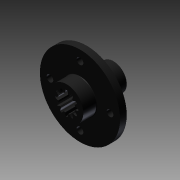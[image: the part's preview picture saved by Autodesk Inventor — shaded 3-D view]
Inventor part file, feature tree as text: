
AUTODESK INVENTOR PART (.ipt)
format: ipt  version: 2011 (Build 150239000, 239)  size: 213,504 bytes
history: native  units: mm (DEFAULTED — no unit token found)
features: sketch x8, extrude x5, hole x3, pattern_circular x1, fillet x1
ambient origin geometry x8: Origin, YZ Plane, XZ Plane, XY Plane, X Axis, Y Axis, Z Axis, Center Point
bodies: Solid1 (feature_tree)
feature tree (18):
  extrude  "Extrusion1"  Depth=76.2mm
  hole  "Mounting Hole"  [1 undecoded]
  pattern_circular  "Circular Pattern1"  Count=4 Angle=360.0deg
  extrude  "Extrusion4"  Depth=12.7mm TaperAngle=0.0deg
  extrude  "Extrusion5"  Depth=29.845mm
  hole  "Hole2"  [1 undecoded]
  extrude  "Extrusion2"  Depth=10.31875mm
  hole  "Hole3"  [1 undecoded]
  extrude  "Extrusion3"  [1 undecoded]
  fillet  "Fillet1"  [1 undecoded]
  sketch  "Sketch1"  dims[d0=6.35mm d1=0.0mm d2=76.2mm]
  sketch  "Sketch2"  dims[d3=0.0mm d4=28.575mm]
  sketch  "Sketch3"  dims[d5=6.35mm d6=12.7mm d7=9.525mm d8=6.35mm d9=14.3117mm d10=19.05mm d11=20.594885mm d12=40.0mm d14=360.0deg]
  sketch  "Sketch4"  dims[d15=31.75mm d17=12.7mm d18=0.0mm]
  sketch  "Sketch5"  dims[d22=12.7mm d23=0.0mm d27=29.845mm]
  sketch  "Sketch6"  dims[d28=25.4mm d29=-0.872665mm d31=16.0mm]
  sketch  "Sketch7"  dims[d32=4.7625mm d33=10.31875mm]
  sketch  "Sketch8"  dims[d34=28.575mm d35=0.0mm d36=9.525mm d37=12.7mm d38=9.525mm d39=6.35mm d40=14.3117mm d41=19.05mm d42=20.594885mm d43=0.508mm d49=16.2mm d50=12.7mm d51=9.525mm d52=6.35mm d53=14.3117mm d54=14.986mm d55=0.0mm]
note: 5 required parameter values undecoded (feature->parameter linkage not recoverable at this tier; creation-order binding heuristic only, values carry confidence <= 0.55)
